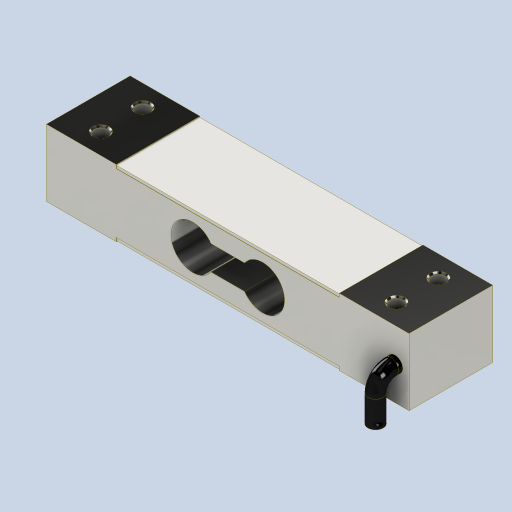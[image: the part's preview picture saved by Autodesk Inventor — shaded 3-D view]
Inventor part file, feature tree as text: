
AUTODESK INVENTOR PART (.ipt)
format: ipt  version: 2023 (Build 270158000, 158)  size: 210,432 bytes
history: native  units: in
note: dims shown in document units (in); Inventor stores cm internally (conversion verified against a paired STEP export)
features: sketch x3, extrude x1, sweep x1, other x1
ambient origin geometry x8: Origin, YZ Plane, XZ Plane, XY Plane, X Axis, Y Axis, Z Axis, Center Point
bodies: Solid1 (feature_tree)
feature tree (6):
  extrude  "Extrusion1"  Depth=0.0394in
  sweep  "Sweep1"
  sketch  "Sketch1"  dims[d0=0.0394in d1=0.0in d2=0.1969in]
  sketch  "Sketch3"  dims[d3=0.2165in d4=0.2756in d5=0.5906in d6=0.0in d7=0.0in d8=0.2165in]
  sketch  "3D Sketch1"
  other  "GLX-150,1"
